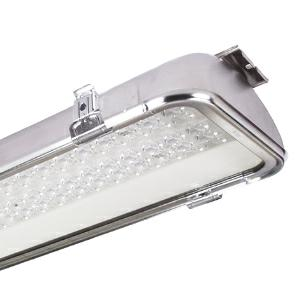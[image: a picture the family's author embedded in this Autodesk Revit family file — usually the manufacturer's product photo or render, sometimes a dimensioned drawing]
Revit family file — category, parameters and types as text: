
# Revit family: 3f_filippi_-_beta_235_93_vt_iperconcentrato_3f_filippi_-_52918_-_beta_235_led_932x40_dali_iperconc_vt_l1265
name_source: partatom
category: Lighting Fixtures
units: mm (PartAtom-declared; Revit-internal decimal feet)

## family parameters
Cut with Voids When Loaded = No
Host = Face
Light Source = No
Part Type = Normal
Room Calculation Point = No
Round Connector Dimension = Use Diameter
Shared = No

## types (1)
- 3F Filippi - Beta 235 93 VT Iperconcentrato (1 x LED, 12139 lm, 80 W, 4000 K)
    Apparent Load = 80 VA
    Approval mark = CE
    CIE Flux Codes = 81 94 99 100 100
    Color Rendering = 80
    Color Temperature = 4000 K
    Control Gear = Electronic transformer
    Default Elevation = 1800 mm
    Description = ILLUMINOTECHNICAL
Luminous efficiency 100% (DLOR 100%, ULOR 0%).
Initial luminous flux of the luminaire 12139 lm.
Symmetrical elliptical hyperconcentrated distribution.
Installation Interdistance Transv.D = 0.35 x hu - Long.D = 0.67 x hu.
Tabular UGR (CIE 117 - 4H-8H; S=0.25H; 70/50/20): RUG 16.9 - 19.4.
Beam angle: 21° - 43°.
Luminous efficacy 152 lm/W.
Lifetime (L93/B10): 30000 h. (tq+25°C)
Lifetime (L90/B10): 50000 h. (tq+25°C)
Lifetime (L85/B10): 80000 h. (tq+25°C)
Lifetime (L80/B10): 100000 h. (tq+25°C)
Lifetime (L85/B10): 50000 h. (tq+45°C)
Sudden decreased luminous flux after 50000 hours: 0% (C0).
Photobiological safety in compliance with IEC/TR 62778: RG0 risk exempt, (IEC 62471).
In compliance with IEC/EN 62722-2-1 - IEC/EN 62717 standards.

SOURCE
2 linear LED modules 40W/840.
Energy efficiency class (UE 2019/2020 - UE 2019/2015): C.
CIE 13.3 Colour rendering index: CRI >80 (R9 <50%).
IES TM-30 Fidelity Index: Rf = 84 Rg = 95.
CCT nominal colour temperature 4000 K.
Colour initial tolerance (MacAdam): SDCM 3.

MECHANICAL
Housing in AISI 304 stainless steel, pressed in one single piece.
VT transparent glass, non-combustible, single-piece perimeter frame in stainless steel.
Oversized gear-tray reflector unit in highly reflective white painted hot-galvanised steel.
Methacrylate (PMMA) lenses with external flat surface.
Stainless steel snap-lock clips for diffuser mounting (safety n° 4 per fixture).
Luminaire with limited surface temperature. - D - (EN 60598-2-24)
Dimensions: 1265x235 mm, height 105 mm. Weight 10.05 kg.
IP65 protection degree.
Mechanical strength to impacts IK09 (10 joule).
Glow-wire test resistance 960°C.

ELECTRICAL
Halogen Free DALI-2 DATI (Parts 251, 252, 253), PUSH-DIM, electronic wiring 230V-50/60Hz, power factor 0.95 at full load, THD <25%, constant output current, class I, 1 driver, 1 DALI addresse.
Power of the luminaire 80 W.
ENEC - CE.
Flicker: <4%.
Luminaire compliant with EN 60598-2-22 for power supply from a centralised emergency system CPSS (Central Power Supply System), not incorporated in the luminaire - high risk areas excluded. The default power and flux are 100% in AC and 15% in DC.
Ambient temperature from -20°C to +45°C.
Temperature class T6 max 85°C.
Quick connection via M25 5P connector with 9-13 mm tightening range.
Relative humidity UR: <85%.

INSTALLATION
Ceiling / Suspended / Wall.
Recommended minimum installation height: 4 metres from the ground.
All accessories dedicated to this product are available on the Catalog and on our website www.3F-Filippi.com.

APPLICATIONS
Dry, dusty indoor environments, subject to occasional water splashes.
Any environments except the ones where the luminaire materials are unsuitable.
Industrial environments, warehouses, environments where security locks are required on all clips, e.g. prisons (on request).
Environments in which it is necessary a total protection against falling fragments (eg environments with foodstuffs or machines with moving parts or with extreme temperature changes), use luminaires with laminated glass.
Tempered glass is not immune to falling fragments from harmless and caused by shocks or exceptionally derived from the tempering process.

LIGHT MANAGEMENT
Recommended minimum setting: 10%.
The luminaire, equipped with (DALI-2 DATI) driver, can be controlled manually with 3F Easy Dim technology or automatically/manually with wired or wireless DALI/D2D control systems.
The D2D driver guarantees interoperability with other devices with the same certification by making the following information available:
Device Data (Part 251), Energy Report (Part 252), Diagnosis & Maintenance (Part 253).
In electrical systems without a regulation system (manual or automatic) and DALI bus, a suitable jumper must be made on the DA-DA terminals of the appliance.

WARNING
Fixture not suitable for cold stores with an ambient temperature <0°C and/or relative humidity >85%.
Luminaire designed for disposal/recycling at end-of-life.
Replaceable (LED only) light source by a professional. Replaceable control gear by a professional.
    Height = 105 mm
    Lamp = 1 x LED
    Lamp Light Flux = 12139 lm
    Lamp Power = 80 W
    Lamp count = 1
    Length = 1265 mm
    Lifetime = 50000 h
    Luminous efficacy = 152 lm/W
    Manufacturer = 3F Filippi
    ModVariant = No
    Model = 3F Filippi - 52918 - Beta 235 LED 932x40 DALI IPERCONC VT L1265
    Mounting Place = Ceiling
    Mounting Type = Pendant
    Number of Poles = 1
    OnlyDefault = Yes
    Power Factor = 1
    Product Name = 3F Filippi - Beta 235 93 VT Iperconcentrato
    Product group = pendant luminaire
    ProductGroupID = 9
    Protection Class = Protection class I
    Protection Degree = IP 65
    RLX_Detail_Level = 1
    RLX_Emergency_Light_Flux = 0 lm
    RLX_Emergency_Type = 0
    RLX_Emergency_Type_DB = No
    RlxData = <blob elided: 95453 chars, md5=f48cc647>
    Socket = socket
    Standby Power = 0 W
    System Light Flux = 12139 lm
    System Power = 80 W
    Type Comments = Product without accessories
    Type Image = 3ffilippi_52918.jpg
    URL = http://relux.com
    VarID = ---
    Voltage = 0 V
    Weight = 0.00 kg
    Width = 235 mm

## geometry (parser evidence)
native form markers: Blend x4, Sweep x10
no freeform markers — native parametric forms only
